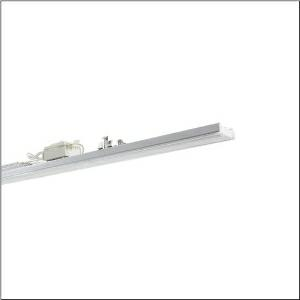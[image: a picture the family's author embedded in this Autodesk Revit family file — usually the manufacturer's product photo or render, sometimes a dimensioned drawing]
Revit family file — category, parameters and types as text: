
# Revit family: licross_21_recessed_ho_52te18mn4e5m
name_source: partatom
category: Lighting Fixtures
units: mm (PartAtom-declared; Revit-internal decimal feet)

## family parameters
Cut with Voids When Loaded = No
Host = Face
Light Source = No
Part Type = Normal
Room Calculation Point = No
Round Connector Dimension = Use Diameter
Shared = No

## types (1)
- --- (1 x LED, 14940 lm, 83.1 W, 4000K)
    Apparent Load = 83 VA
    CIE Flux Codes = 75 94 99 100 100
    Color Rendering = 80
    Color Temperature = 4000K
    Default Elevation = 1800 mm
    Description = Licross 21 Recessed HO, luminaire insert, of sheet steel, galvanised, coil coated, white, length: 1.500mm, width: 66mm, height: 67mm, LED rated luminous flux: 14.940lm, light colour: 840, SDCM (Standard Deviation of Colour Matching)MacAdam ≤ 3 SDCM (initial), control gear: ON/OFF Multilumen, with plug, 3-pole, with phase selection, mains connection: 220..240V, AC, 50/60Hz, rated input power: 83W, internal wiring halogen-free, primary light control with lens, of plastic, primary optical cover: cover, of PMMA, light emission: direct distribution, primary light characteristic: symmetric, protection rating (complete): IP54, insulation class (complete): insulation class I (protective earthing), certification: CE, ENEC, VDE, UKCA, protection symbol: D if used in an environment with non-conductive dust loads with corresponding accessories, impact resistance: IK06, permissible ambient temperature for indoor applications: -35..+30°C, corresponds to IFS (International Featured Standards) requirements for safety and quality in the food industry, reducing of maximum allowable ambient temperature of 5°C with ceiling mounting, LABS conformity tested according to VDMA 24364:2018-05, The light source and the operating device comply with the requirements of the Ecodesign Regulation (EU) 2019/2020 and are replaceable in accordance with this regulation, packaging unit: 1 piece
    Height = 58 mm
    Lamp = 1 x LED
    Lamp Light Flux = 14940 lm
    Lamp Power = 83.1 W
    Lamp count = 1
    Length = 1500 mm
    Luminous efficacy = 180 lm/W
    Manufacturer = Siteco
    ModVariant = No
    Model = 52TE18MN4E5M
    Mounting Place = Ceiling
    Mounting Type = Pendant
    Number of Poles = 1
    OnlyDefault = Yes
    Power Factor = 1
    Product Name = Licross 21 Recessed HO
    Product group = luminaire insert | ceiling pendant
    ProductGroupID = 901
    Protection Class = Protection class I
    Protection Degree = IP 54
    RLX_Detail_Level = 1
    RLX_Emergency_Light_Flux = 0 lm
    RLX_Emergency_Type = 0
    RLX_Emergency_Type_DB = No
    RlxData = <blob elided: 22517 chars, md5=a1cebab3>
    Socket = socket
    Standby Power = 0 W
    System Light Flux = 14940 lm
    System Power = 83 W
    Type Comments = factory setting: luminous flux: 100 % | (A | C | E) | 195 mA
    Type Image = l_1296930.jpg
    URL = http://relux.com
    VarID = @adj_107915
    Voltage = 0 V
    Weight = 0.00 kg
    Width = 66 mm

## geometry (parser evidence)
native form markers: Blend x4, Sweep x11
no freeform markers — native parametric forms only
